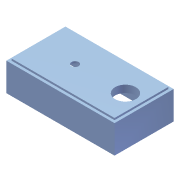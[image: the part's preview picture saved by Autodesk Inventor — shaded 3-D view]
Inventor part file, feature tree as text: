
AUTODESK INVENTOR PART (.ipt)
format: ipt  version: 2012 (Build 160160000, 160)  size: 150,528 bytes
history: native  units: mm
features: extrude x7, sketch x7, projected_geometry x1
ambient origin geometry x8: Origin, YZ Plane, XZ Plane, XY Plane, X Axis, Y Axis, Z Axis, Center Point
bodies: Solid1 (feature_tree)
feature tree (15):
  extrude  "Extrusion1"  Depth=66.2mm
  extrude  "Extrusion2"  Depth=33.1mm
  extrude  "Extrusion3"  Depth=31.5mm TaperAngle=0.0deg
  extrude  "Extrusion4"  Depth=8.1mm
  extrude  "Extrusion5"  Depth=30.2mm
  extrude  "Extrusion6"  Depth=18.0mm
  extrude  "Extrusion7"  Depth=23.282852mm
  sketch  "Sketch1"  dims[d0=121.2mm d1=66.2mm]
  sketch  "Sketch2"  dims[d2=60.6mm d3=33.1mm]
  sketch  "Sketch3"  dims[d4=2.9mm d5=31.5mm d6=0.0mm]
  projected_geometry  "Projected Loop1"
  sketch  "Sketch4"  dims[d7=2.1mm d8=0.0mm d9=8.1mm]
  sketch  "Sketch5"  dims[d10=41.0mm d11=30.2mm]
  sketch  "Sketch6"  dims[d12=30.2mm d13=18.0mm]
  sketch  "Sketch7"  dims[d14=2.1mm d15=0.0mm d16=23.282852mm d17=26.282852mm d18=6.0mm d19=0.0mm d20=9.1mm d21=31.8mm d22=0.0mm d23=2.4mm d24=0.0mm d25=5.1mm d26=29.0mm d27=0.0mm d28=60.4mm d29=24.6mm d30=65.6mm d31=8.1mm d32=41.0mm d33=14.05mm d34=20.0mm d36=22.0mm d37=8.1mm d39=12.0mm d40=0.0mm]
